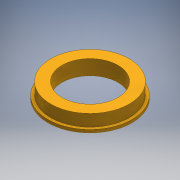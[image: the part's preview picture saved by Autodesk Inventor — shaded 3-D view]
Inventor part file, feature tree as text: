
AUTODESK INVENTOR PART (.ipt)
format: ipt  version: 2016 (Build 200138000, 138)  size: 110,080 bytes
history: native  units: mm
features: extrude x2, other x1, sketch x1
ambient origin geometry x8: Origin, YZ Plane, XZ Plane, XY Plane, X Axis, Y Axis, Z Axis, Center Point
bodies: Body1 (feature_tree)
feature tree (4):
  other  "ソリッド1"
  sketch  "スケッチ1"
  extrude  "押し出し1"  Depth=15.0mm
  extrude  "押し出し2"  Depth=21.0mm
